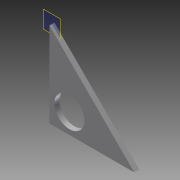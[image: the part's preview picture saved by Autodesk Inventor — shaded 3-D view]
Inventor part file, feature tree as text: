
AUTODESK INVENTOR PART (.ipt)
format: ipt  version: 2013 (Build 170138000, 138)  size: 75,264 bytes
history: native  units: in
note: dims shown in document units (in); Inventor stores cm internally (conversion verified against a paired STEP export)
features: sketch x1, extrude x1, hole x1, plane x1
ambient origin geometry x8: Origin, YZ Plane, XZ Plane, XY Plane, X Axis, Y Axis, Z Axis, Center Point
bodies: Solid1 (feature_tree)
feature tree (4):
  sketch  "Sketch1"  dims[d0=4.24in d1=1.0in d2=1.0in d3=0.25in d4=0.0in d5=1.5in d6=0.75in d7=0.375in d8=0.25in d9=0.5635in d10=1.0in d11=0.8108in]
  extrude  "Extrusion1"  Depth=1.0in
  hole  "Hole1"  [1 undecoded]
  plane  "Work Plane1"
note: 1 required parameter value undecoded (feature->parameter linkage not recoverable at this tier; creation-order binding heuristic only, values carry confidence <= 0.55)
